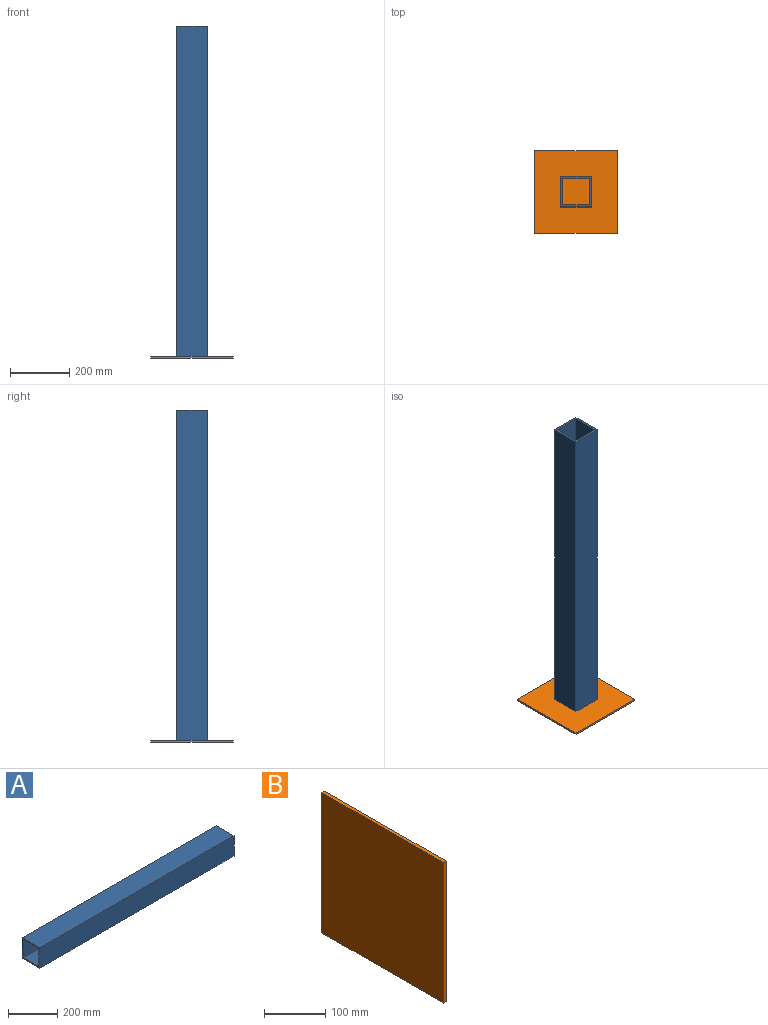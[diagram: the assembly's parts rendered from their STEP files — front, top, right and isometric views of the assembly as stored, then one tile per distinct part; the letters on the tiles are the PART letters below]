
ASSEMBLY  parts=2 mates=1
PART A: 10 faces, bbox 1117.6x101.6x101.6 mm
  f0: plane 1117.6x88.9mm, normal (0,-1,0), area 99354.6mm2, adj f1,f7,f8,f9
  f1: plane 1117.6x88.9mm, normal (0,0,1), area 99354.6mm2, adj f0,f2,f8,f9
  f2: plane 1117.6x88.9mm, normal (0,1,0), area 99354.6mm2, adj f1,f7,f8,f9
  f3: plane 1117.6x101.6mm, normal (0,-1,0), area 113548.2mm2, adj f4,f6,f8,f9
  f4: plane 1117.6x101.6mm, normal (0,0,-1), area 113548.2mm2, adj f3,f5,f8,f9
  f5: plane 1117.6x101.6mm, normal (0,1,0), area 113548.2mm2, adj f4,f6,f8,f9
  f6: plane 1117.6x101.6mm, normal (0,0,1), area 113548.2mm2, adj f3,f5,f8,f9
  f7: plane 1117.6x88.9mm, normal (0,0,-1), area 99354.6mm2, adj f0,f2,f8,f9
  f8: plane 101.6x101.6mm, normal (1,0,0), area 2419.3mm2, adj f0,f1,f2,f3,f4,f5,f6,f7
  f9: plane 101.6x101.6mm, normal (-1,0,0), area 2419.3mm2, adj f0,f1,f2,f3,f4,f5,f6,f7
PART B: 6 faces, bbox 6.4x279.4x279.4 mm
  f0: plane 279.4x6.35mm, normal (0,-1,0), area 1774.2mm2, adj f1,f3,f4,f5
  f1: plane 279.4x6.35mm, normal (0,0,-1), area 1774.2mm2, adj f0,f2,f4,f5
  f2: plane 279.4x6.35mm, normal (0,1,0), area 1774.2mm2, adj f1,f3,f4,f5
  f3: plane 279.4x6.35mm, normal (0,0,1), area 1774.2mm2, adj f0,f2,f4,f5
  f4: plane 279.4x279.4mm, normal (1,0,0), area 78064.4mm2, adj f0,f1,f2,f3
  f5: plane 279.4x279.4mm, normal (-1,0,0), area 78064.4mm2, adj f0,f1,f2,f3
PLACE A rot(axis=(0,-1,0),90deg) t=(50.8,-50.8,-7715.25)mm
PLACE B rot(axis=(0,-1,0),90deg) t=(723.9,-139.7,0)mm
MATE fastened A.f9 <-> B.f4  axis (0,0,-1) through (0,0,6.35)mm
